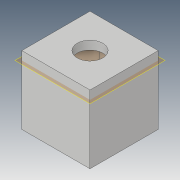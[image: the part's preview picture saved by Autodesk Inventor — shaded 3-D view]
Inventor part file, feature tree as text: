
AUTODESK INVENTOR PART (.ipt)
format: ipt  version: 2019 (Build 230136000, 136)  size: 102,912 bytes
history: native  units: mm
features: extrude x2, sketch x2, plane x1
ambient origin geometry x8: Origin, YZ Plane, XZ Plane, XY Plane, X Axis, Y Axis, Z Axis, Center Point
bodies: Solid1 (feature_tree)
feature tree (5):
  extrude  "Extrusion1"  Depth=6.0mm
  plane  "Work Plane1"
  extrude  "Extrusion2"  Depth=3.15mm
  sketch  "Sketch1"  dims[d0=4.5mm d1=6.0mm]
  sketch  "Sketch2"  dims[d2=6.0mm d3=6.0mm d4=6.0mm d5=12.0mm d6=0.0mm d7=-1.5mm d8=7.5mm d9=3.15mm d10=0.0mm]
